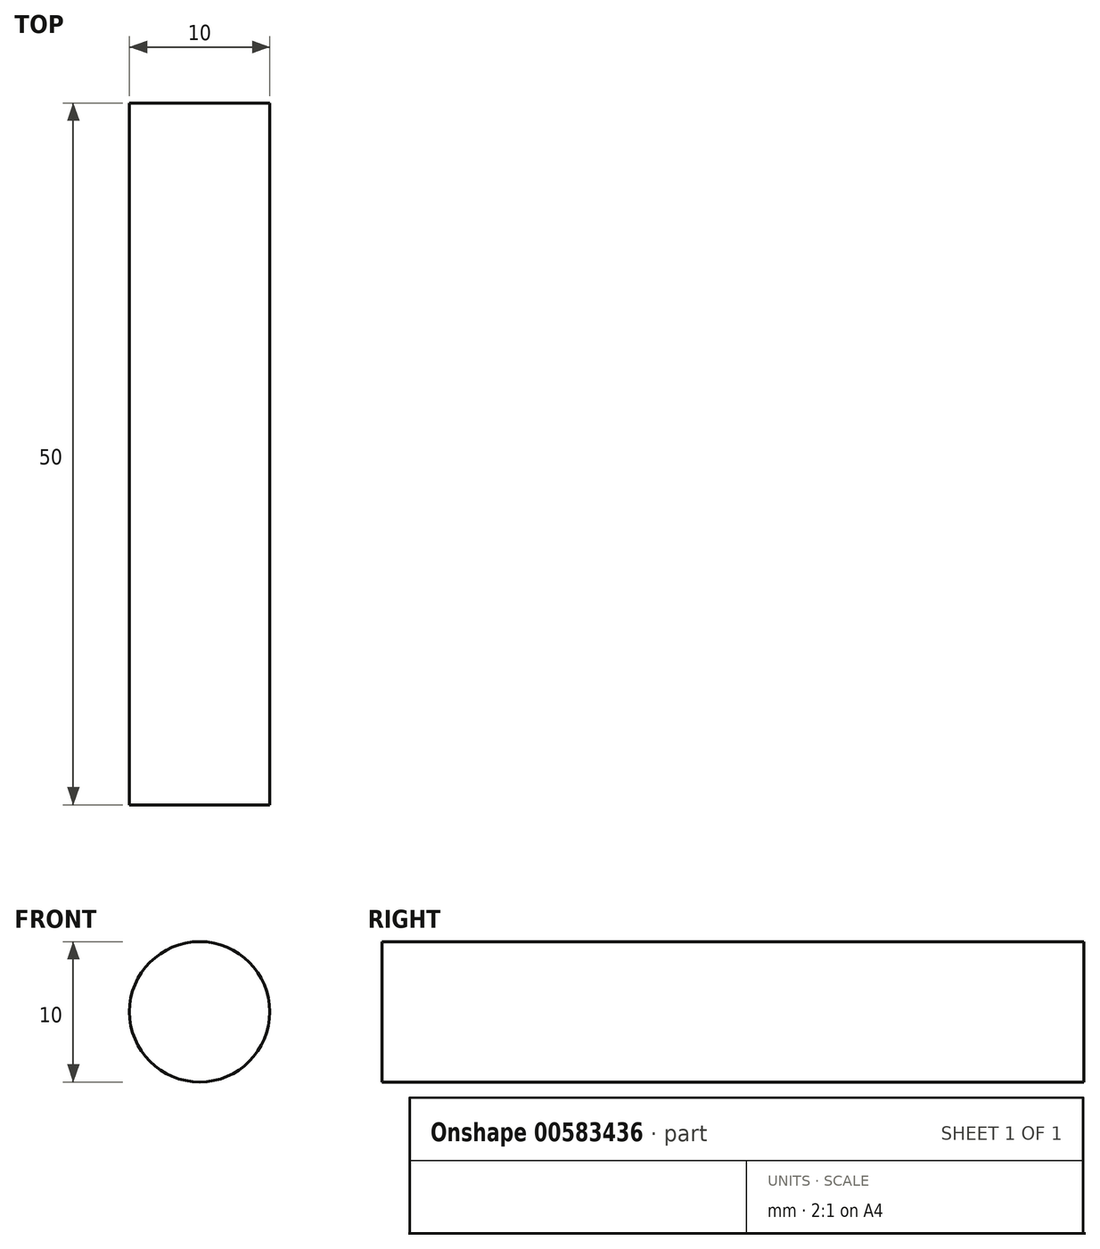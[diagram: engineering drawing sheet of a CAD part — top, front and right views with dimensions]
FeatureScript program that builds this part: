
annotation { "Feature Type Name" : "Feature", "Feature Type Description" : "" }
export const myFeature = defineFeature(function(context is Context, id is Id, definition is map)
    precondition{}
    {
        {
            var Q0;
            Q0=qCreatedBy(makeId("Front.planeOp"),FACE);
            var sketch = newSketch(context, id + "F0", { "sketchPlane" : qUnion([Q0])});
            skCircle(sketch, "E0", {"center": v(0, 0) * mm, "radius": 5 * mm});
            skSolve(sketch);
        }
        {
            var Q0;
            Q0=makeQuery(id+"F0.imprint","IMPRINT",FACE,{"disambiguationData":[TD([[makeQuery(id+"F0.imprint","IMPRINT",EDGE,{"derivedFrom":sQuery(id+"F0.wireOp",EDGE,"E0")}),1.0]])]});
            extrude(context, id + "F1", {"entities" : qUnion([Q0]), "depth" : 50 * mm, "offsetDistance" : 25 * mm});
        }
    });
